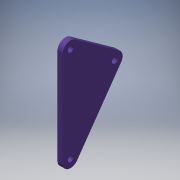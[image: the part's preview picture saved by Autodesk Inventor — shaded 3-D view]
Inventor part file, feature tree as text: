
AUTODESK INVENTOR PART (.ipt)
format: ipt  version: 2017 SP1 (Build 210196100, 196)  size: 114,688 bytes
history: native  units: in
note: dims shown in document units (in); Inventor stores cm internally (conversion verified against a paired STEP export)
features: extrude x1, sketch x1
ambient origin geometry x8: Origin, YZ Plane, XZ Plane, XY Plane, X Axis, Y Axis, Z Axis, Center Point
bodies: Solid1 (feature_tree)
feature tree (2):
  extrude  "Extrusion1"  Depth=0.25in
  sketch  "Sketch1"  dims[d0=1.0in d1=0.26in d2=0.548in d3=1.25in d4=1.5in d5=3.0in d6=0.375in d7=0.25in d8=0.0in]
